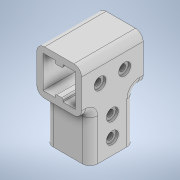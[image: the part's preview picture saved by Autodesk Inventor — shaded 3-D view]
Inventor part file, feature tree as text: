
AUTODESK INVENTOR PART (.ipt)
format: ipt  version: 2021 (Build 250183000, 183)  size: 301,056 bytes
history: native  units: mm
features: extrude x5, sketch x5, projected_geometry x4, other x2, mirror x1, fillet x1
ambient origin geometry x8: Origin, YZ Plane, XZ Plane, XY Plane, X Axis, Y Axis, Z Axis, Center Point
bodies: Body1 (feature_tree)
feature tree (18):
  other  "솔리드1"
  extrude  "돌출1"  Depth=21.0mm
  extrude  "돌출2"  Depth=5.2mm
  extrude  "돌출3"  Depth=2.0mm
  extrude  "돌출4"  Depth=4.0mm
  other  "작업 평면1"
  mirror  "미러1"
  fillet  "모깎기1"  Radius=40.0mm
  extrude  "돌출5"  Depth=21.0mm
  sketch  "스케치1"
  sketch  "스케치2"
  sketch  "스케치3"
  projected_geometry  "투영된 루프1"
  projected_geometry  "투영된 루프2"
  sketch  "스케치4"
  projected_geometry  "투영된 루프3"
  sketch  "스케치5"
  projected_geometry  "투영된 루프4"
